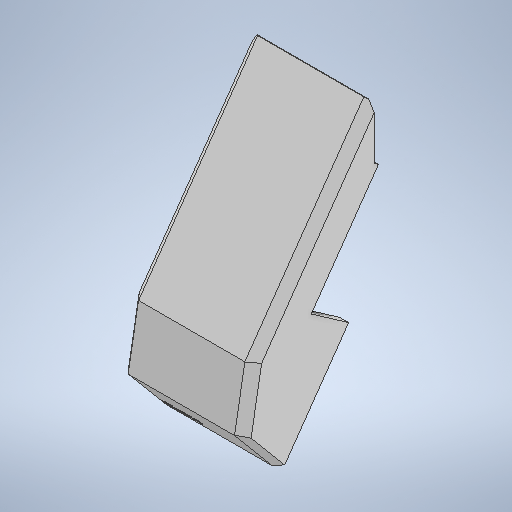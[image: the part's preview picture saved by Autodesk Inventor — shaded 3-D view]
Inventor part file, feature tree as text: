
AUTODESK INVENTOR PART (.ipt)
format: ipt  version: 2025.2 (Build 292293000, 293)  size: 1,497,088 bytes
history: native  units: in
note: dims shown in document units (in); Inventor stores cm internally (conversion verified against a paired STEP export)
features: sketch x48, extrude x43, projected_geometry x14, plane x10, move_body x1, chamfer x1, fillet x1, thicken_offset x1, hole x1
ambient origin geometry x8: Origin, YZ Plane, XZ Plane, XY Plane, X Axis, Y Axis, Z Axis, Center Point
bodies: Solid1 (feature_tree)
feature tree (120):
  extrude  "Extrusion1"  Depth=0.1969in TaperAngle=0.0deg
  move_body  "Move Body1"
  plane  "Work Plane1"
  sketch  "Sketch5"  dims[d5=1.7717in d6=1.7717in d7=1.7717in d8=1.7717in d9=0.8108in d10=90.0deg d11=0.0787in d12=0.3701in d13=0.4252in d14=0.1362in d15=-0.0984in d16=-0.0591in d17=0.0in]
  plane  "Work Plane2"
  extrude  "Extrusion4"  TaperAngle=0.0deg  [1 undecoded]
  extrude  "Extrusion6"  Depth=0.2405in
  extrude  "Extrusion8"  Depth=2.5591in TaperAngle=0.0deg
  chamfer  "Chamfer1"  [1 undecoded]
  extrude  "Extrusion11"  Depth=0.2362in
  plane  "Work Plane3"
  plane  "Work Plane7"
  extrude  "Extrusion22"  Depth=0.0787in TaperAngle=0.0deg
  extrude  "Extrusion25"  Depth=0.5027in
  extrude  "Extrusion26"  Depth=0.5027in
  sketch  "Sketch33"  dims[d96=0.2362in d97=0.0in d100=3.6403in]
  extrude  "Extrusion27"  Depth=0.2362in TaperAngle=0.0deg
  extrude  "Extrusion28"  Depth=3.6403in
  sketch  "Sketch36"  dims[d123=0.9331in d124=0.9712in d125=0.0in]
  extrude  "Extrusion29"  Depth=1.9685in
  extrude  "Extrusion30"  Depth=0.1575in
  extrude  "Extrusion31"  Depth=0.9712in TaperAngle=0.0deg
  sketch  "Sketch39"  dims[d138=0.4331in d139=0.1181in d140=0.0in]
  extrude  "Extrusion32"  Depth=11.3469in TaperAngle=0.0deg
  fillet  "Fillet1"  Radius=11.3469in
  extrude  "Extrusion33"  Depth=0.4331in
  extrude  "Extrusion34"  Depth=0.1181in TaperAngle=0.0deg
  extrude  "Extrusion35"  Depth=0.0787in
  plane  "Work Plane8"
  sketch  "Sketch45"  dims[d160=0.1181in d161=0.0in d162=0.1969in d163=0.0in d164=0.1181in d165=0.0in]
  extrude  "Extrusion37"  Depth=0.2756in
  extrude  "Extrusion38"  Depth=0.1181in TaperAngle=0.0deg
  extrude  "Extrusion40"  Depth=0.5906in
  extrude  "Extrusion41"  Depth=0.1181in TaperAngle=0.0deg
  extrude  "Extrusion43"  Depth=4.7244in TaperAngle=0.0deg
  extrude  "Extrusion44"  Depth=0.7313in TaperAngle=0.0deg
  extrude  "Extrusion46"  TaperAngle=0.0deg  [1 undecoded]
  extrude  "Extrusion48"  Depth=1.1024in
  extrude  "Extrusion50"  Depth=0.0394in TaperAngle=0.0deg
  extrude  "Extrusion51"  Depth=5.8937in TaperAngle=0.0deg
  extrude  "Extrusion53"  Depth=2.3622in TaperAngle=0.0deg
  plane  "Work Plane9"
  plane  "Work Plane12"
  extrude  "Extrusion65"  Depth=0.1969in
  plane  "Work Plane13"
  extrude  "Extrusion67"  TaperAngle=60.0deg  [1 undecoded]
  plane  "Work Plane14"
  extrude  "Extrusion68"  Depth=0.7902in
  extrude  "Extrusion69"  Depth=0.3436in
  extrude  "Extrusion70"  Depth=0.2362in
  sketch  "Sketch84"  dims[d298=0.2362in d299=0.0in d300=0.2362in d301=0.0in]
  extrude  "Extrusion71"  TaperAngle=0.0deg  [1 undecoded]
  extrude  "Extrusion72"  Depth=0.2362in TaperAngle=0.0deg
  extrude  "Extrusion73"  TaperAngle=90.0deg  [1 undecoded]
  extrude  "Extrusion74"  Depth=0.2362in TaperAngle=0.0deg
  extrude  "Extrusion75"  TaperAngle=0.0deg  [1 undecoded]
  extrude  "Extrusion76"  Depth=0.0787in
  thicken_offset  "Thicken1"
  extrude  "Extrusion78"  TaperAngle=90.0deg  [1 undecoded]
  plane  "Work Plane15"
  extrude  "Extrusion79"  Depth=0.0787in
  extrude  "Extrusion80"  Depth=0.0787in TaperAngle=0.0deg
  extrude  "Extrusion81"  TaperAngle=0.0deg  [1 undecoded]
  sketch  "Sketch1"  dims[d1=0.5512in d2=0.1969in d3=0.0in]
  sketch  "Sketch6"  dims[d18=0.2749in d24=0.2405in]
  sketch  "Sketch8"  dims[d25=2.7559in d26=0.0in d29=2.5591in d30=0.0in d36=0.0in d37=0.0in]
  sketch  "Sketch12"  dims[d42=0.2362in d43=0.2362in]
  sketch  "Sketch15"  dims[d52=0.2362in d53=0.0787in d54=45.0deg d55=0.1969in d56=0.0in]
  sketch  "Sketch28"  dims[d76=0.5027in d77=0.5027in]
  sketch  "Sketch31"  dims[d78=0.5027in d79=0.5027in]
  sketch  "Sketch32"  dims[d83=0.0in d84=0.0in d94=0.2362in d95=0.0in]
  sketch  "Sketch34"  dims[d101=2.7717in d112=1.9685in]
  sketch  "Sketch35"  dims[d113=0.6299in d114=0.0in d115=0.1575in d117=0.1575in d121=1.9685in d122=0.7874in]
  sketch  "Sketch37"  dims[d126=0.5906in d127=0.0in d128=11.3469in d129=0.0in d130=11.3469in d131=0.0in]
  sketch  "Sketch38"  dims[d136=0.4331in d137=0.4331in]
  sketch  "Sketch40"  dims[d141=0.6299in d142=0.0787in]
  sketch  "Sketch41"  dims[d147=0.2756in d149=0.2756in]
  sketch  "Sketch42"  dims[d150=0.0in d151=0.0in d154=0.1181in d155=0.0in]
  sketch  "Sketch44"  dims[d156=0.1181in d157=0.0in d158=0.5906in]
  projected_geometry  "Projected Loop2"
  projected_geometry  "Projected Loop3"
  projected_geometry  "Projected Loop5"
  sketch  "Sketch47"  dims[d168=0.5906in d169=0.0in d170=4.7244in d171=0.0in]
  sketch  "Sketch49"  dims[d174=0.0in d175=0.0in d176=0.7313in d177=0.0in]
  sketch  "Sketch50"  dims[d186=0.0in d187=0.0in d188=0.0in d189=0.0in]
  sketch  "Sketch52"  dims[d194=0.0in d195=0.0in d196=1.1024in]
  sketch  "Sketch53"  dims[d197=0.5906in d200=0.0394in d201=0.0in]
  sketch  "Sketch56"  dims[d218=0.0in d219=0.0in d220=5.8937in d221=0.0in]
  sketch  "Sketch59"  dims[d233=0.9963in d234=2.3622in d235=0.0in]
  sketch  "Sketch60"  dims[d266=0.1378in d268=0.1969in]
  sketch  "Sketch61"  dims[d269=0.1378in d270=60.0deg]
  sketch  "Sketch63"  dims[d271=4.5565in d272=0.0in d277=0.7902in]
  projected_geometry  "Projected Loop8"
  sketch  "Sketch76"  dims[d278=0.5906in d279=1.378in d280=0.0in d281=0.0in d282=0.3436in]
  sketch  "Sketch78"  dims[d283=1.378in d284=0.9843in d285=0.0in d286=0.0in d287=0.2362in]
  projected_geometry  "Projected Loop14"
  sketch  "Sketch79"  dims[d288=0.0in d289=0.0in d290=0.0in d291=0.0in]
  projected_geometry  "Projected Loop15"
  projected_geometry  "Projected Loop16"
  projected_geometry  "Projected Loop17"
  sketch  "Sketch80"  dims[d292=0.5894in d293=0.2362in d294=0.0in]
  projected_geometry  "Projected Loop18"
  projected_geometry  "Projected Loop20"
  sketch  "Sketch83"  dims[d295=0.2362in d296=0.0in d297=90.0deg]
  projected_geometry  "Projected Loop22"
  sketch  "Sketch85"  dims[d302=0.0787in d303=0.0in d304=0.0in d305=0.0in]
  sketch  "Sketch86"  dims[d306=0.0787in d307=0.0787in]
  sketch  "Sketch87"  dims[d314=0.1181in d315=0.0in d316=90.0deg]
  sketch  "Sketch88"  dims[d317=0.0787in d318=0.0787in]
  sketch  "Sketch89"  dims[d319=0.0787in d320=1.7037in d321=0.0in]
  sketch  "Sketch90"  dims[d322=0.0787in d323=0.0in d324=0.0in]
  projected_geometry  "Projected Loop23"
  sketch  "Sketch92"  dims[d325=0.0in d326=0.0in d38=0.0197in]
  projected_geometry  "Projected Loop25"
  projected_geometry  "Projected Loop26"
  sketch  "Sketch94"  dims[d39=0.0344in]
  sketch  "Sketch95"  dims[d57=0.0197in]
  sketch  "Sketch96"  dims[d58=0.0344in d59=0.0197in d60=0.0344in d81=0.0197in d82=0.0344in d159=0.0344in d178=0.0in d179=0.0in d180=0.0in d181=0.0in d202=0.0197in d203=0.0344in d222=0.0197in d223=0.0344in]
  sketch  "Sketch2"  dims[d4=0.315in]
  hole  "Hole1"  [1 undecoded]
note: 10 required parameter values undecoded (feature->parameter linkage not recoverable at this tier; creation-order binding heuristic only, values carry confidence <= 0.55)
